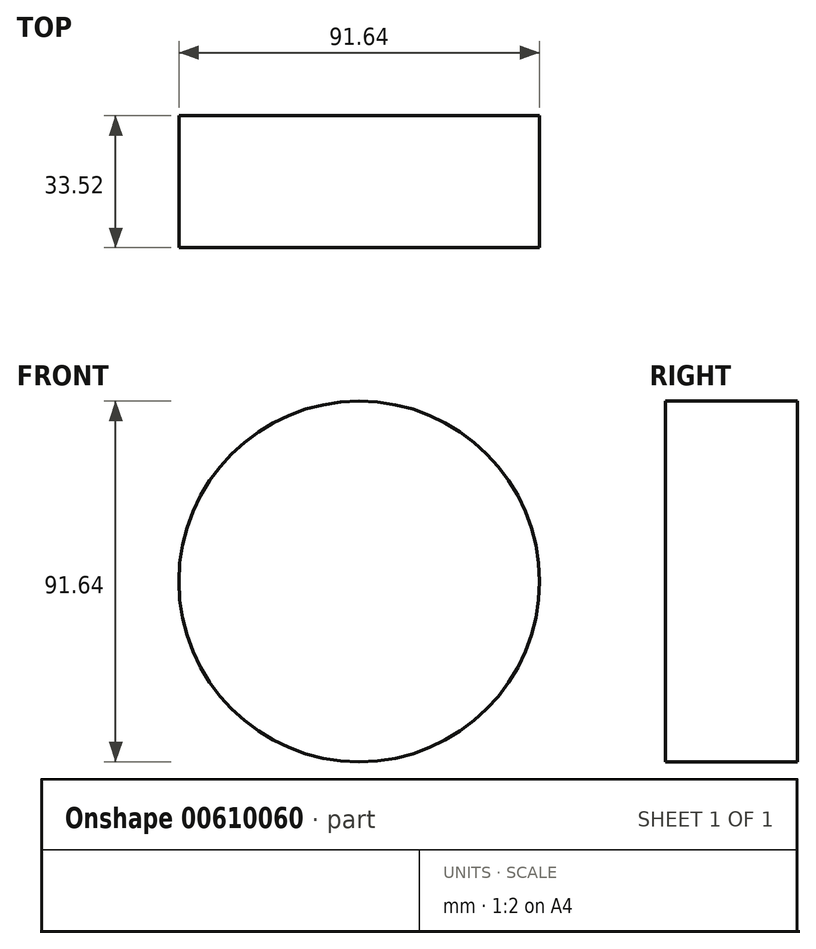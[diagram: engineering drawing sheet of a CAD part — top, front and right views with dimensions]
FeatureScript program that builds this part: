
annotation { "Feature Type Name" : "Feature", "Feature Type Description" : "" }
export const myFeature = defineFeature(function(context is Context, id is Id, definition is map)
    precondition{}
    {
        {
            var Q0;
            Q0=qCreatedBy(makeId("Top.planeOp"),FACE);
            var sketch = newSketch(context, id + "F0", { "sketchPlane" : qUnion([Q0])});
            skLineSegment(sketch, "E0.bottom", {"start": v(0, 0) * mm, "end": v(45.82, 0) * mm});
            skLineSegment(sketch, "E0.top", {"start": v(0, 33.52) * mm, "end": v(45.82, 33.52) * mm});
            skLineSegment(sketch, "E0.left", {"start": v(0, 0) * mm, "end": v(0, 33.52) * mm});
            skLineSegment(sketch, "E0.right", {"start": v(45.82, 0) * mm, "end": v(45.82, 33.52) * mm});
            skSolve(sketch);
        }
        {
            var Q0;
            Q0=makeQuery(id+"F0.imprint","IMPRINT",FACE,{"disambiguationData":[TD([[makeQuery(id+"F0.imprint","IMPRINT",EDGE,{"derivedFrom":sQuery(id+"F0.wireOp",EDGE,"E0.bottom")}),1.0]])]});
            var Q1;
            Q1=sQuery(id+"F0.wireOp",EDGE,"E0.left");
            revolve(context, id + "F1", {"entities" : qUnion([Q0]), "axis" : qUnion([Q1]), "revolveType" : RevolveType.FULL});
        }
    });
